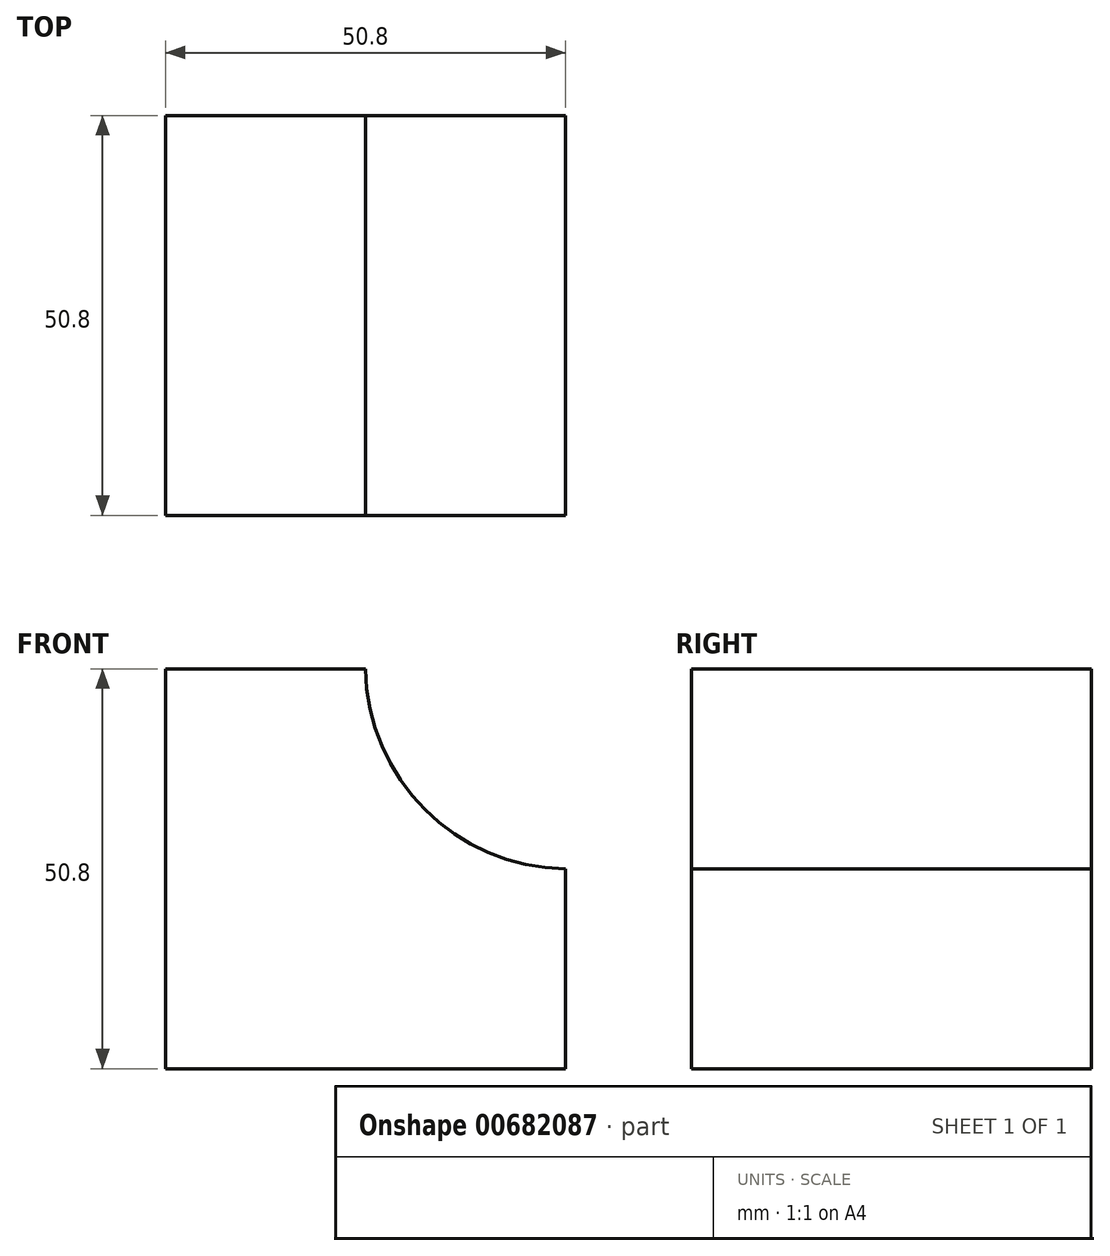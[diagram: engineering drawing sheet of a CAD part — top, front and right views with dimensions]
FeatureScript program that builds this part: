
annotation { "Feature Type Name" : "Feature", "Feature Type Description" : "" }
export const myFeature = defineFeature(function(context is Context, id is Id, definition is map)
    precondition{}
    {
        {
            var Q0;
            Q0=qCreatedBy(makeId("Front.planeOp"),FACE);
            var sketch = newSketch(context, id + "F0", { "sketchPlane" : qUnion([Q0])});
            skLineSegment(sketch, "E0", {"start": v(0, 25.4) * mm, "end": v(0, 0) * mm});
            skLineSegment(sketch, "E1", {"start": v(0, 0) * mm, "end": v(-50.8, 0) * mm});
            skLineSegment(sketch, "E2", {"start": v(-50.8, 0) * mm, "end": v(-50.8, 50.8) * mm});
            skLineSegment(sketch, "E3", {"start": v(-50.8, 50.8) * mm, "end": v(-25.4, 50.8) * mm});
            skArc(sketch, "E4", {"start": v(-25.4, 50.8) * mm, "mid": v(-17.87, 32.93) * mm, "end": v(0, 25.4) * mm});
            skSolve(sketch);
        }
        {
            var Q0;
            Q0 = qSketchRegion(id + "F0", true);
            extrude(context, id + "F1", {"entities" : qUnion([Q0]), "depth" : 50.8 * mm, "offsetDistance" : 25.4 * mm});
        }
    });
